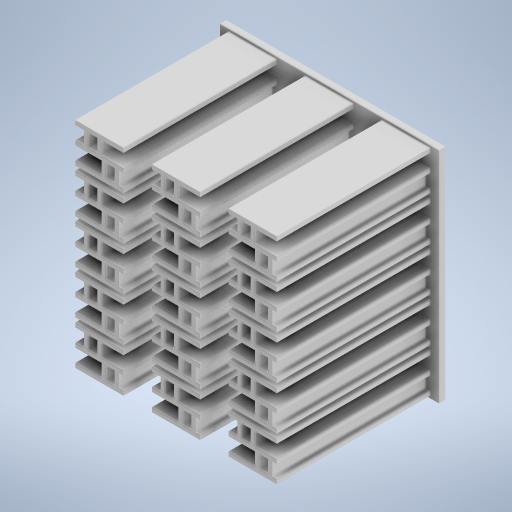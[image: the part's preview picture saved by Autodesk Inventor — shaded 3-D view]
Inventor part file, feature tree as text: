
AUTODESK INVENTOR PART (.ipt)
format: ipt  version: 2023 (Build 270158000, 158)  size: 756,736 bytes
history: native  units: mm
features: projected_geometry x4, extrude x2, sketch x2, pattern_linear x1
ambient origin geometry x8: Origin, YZ Plane, XZ Plane, XY Plane, X Axis, Y Axis, Z Axis, Center Point
bodies: Solid1 (feature_tree)
feature tree (9):
  extrude  "Extrusion1"  Depth=22.0mm
  pattern_linear  "Rectangular Pattern1"  Spacing1=2.0mm  [1 undecoded]
  extrude  "Extrusion3"  Depth=4.0mm
  sketch  "Sketch1"  dims[d0=2.0mm d1=22.0mm]
  sketch  "Sketch4"  dims[d2=2.0mm d3=2.0mm d4=4.0mm d5=4.0mm d7=2.0mm d8=2.0mm d9=2.0mm d10=2.0mm d13=4.0mm d14=2.0mm d15=2.0mm d16=2.0mm d17=2.0mm d18=2.0mm d20=2.0mm d21=2.0mm d22=2.0mm d23=6.0mm d24=6.0mm d25=6.0mm d26=2.0mm d27=6.0mm d28=6.0mm d29=1.0mm d30=2.0mm d31=2.0mm d32=1.0mm d33=70.0mm d34=0.0mm d41=30.0mm d43=35.0mm d44=50.0mm d46=20.0mm d47=1.0mm d48=1.0mm d49=4.0mm d50=4.0mm d51=3.0mm d52=0.0mm]
  projected_geometry  "Projected Loop2"
  projected_geometry  "Projected Loop3"
  projected_geometry  "Projected Loop4"
  projected_geometry  "Projected Loop5"
note: 1 required parameter value undecoded (feature->parameter linkage not recoverable at this tier; creation-order binding heuristic only, values carry confidence <= 0.55)
